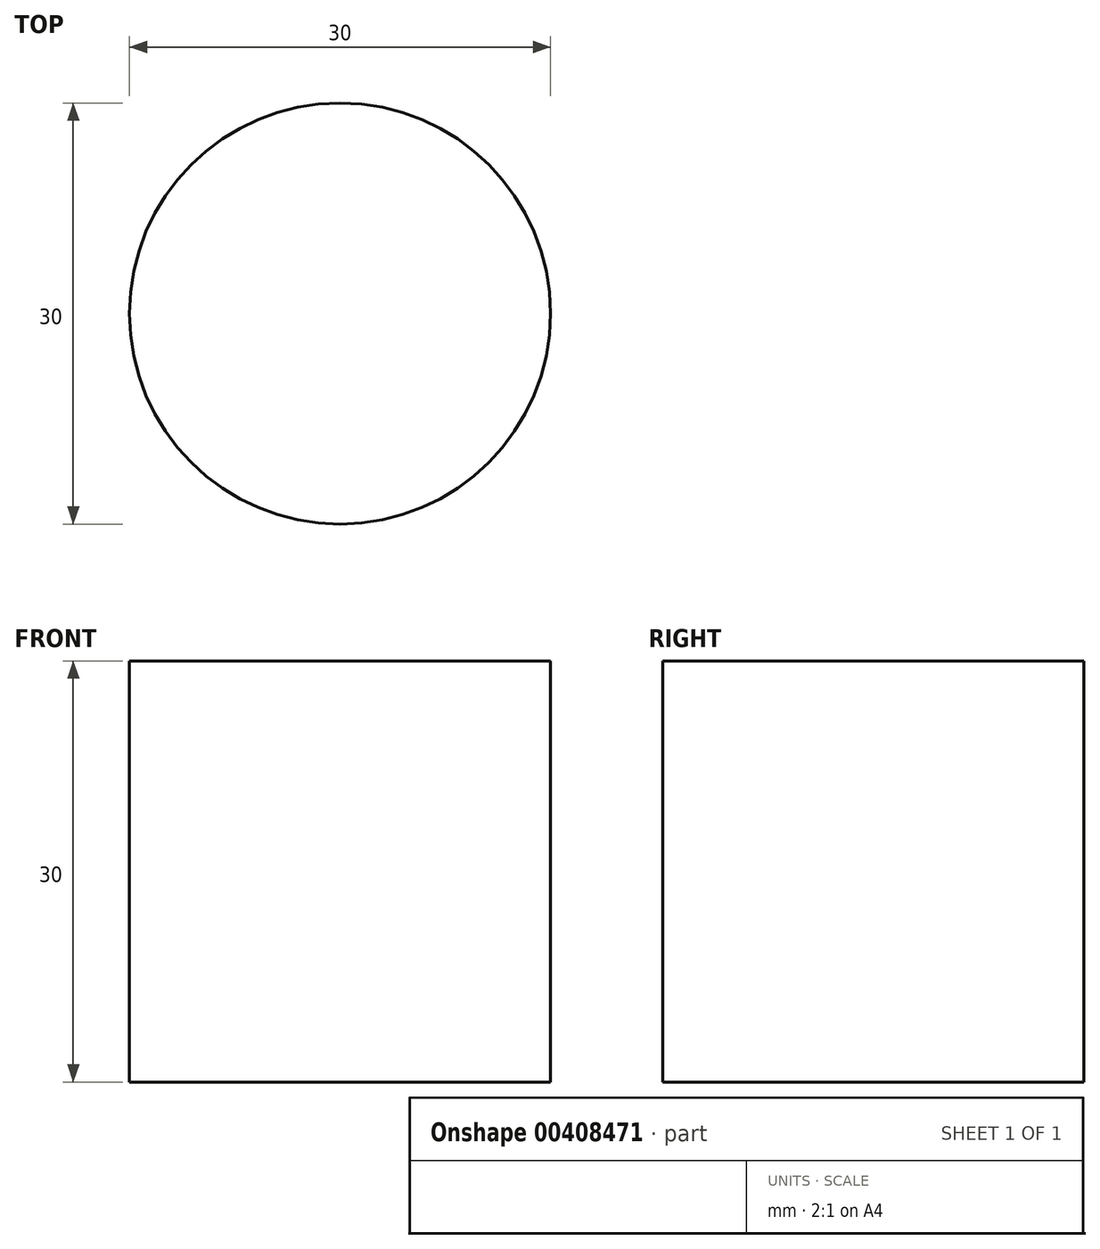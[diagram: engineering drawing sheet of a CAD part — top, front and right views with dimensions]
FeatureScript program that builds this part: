
annotation { "Feature Type Name" : "Feature", "Feature Type Description" : "" }
export const myFeature = defineFeature(function(context is Context, id is Id, definition is map)
    precondition{}
    {
        {
            var Q0;
            Q0=qCreatedBy(makeId("Top.planeOp"),FACE);
            var sketch = newSketch(context, id + "F0", { "sketchPlane" : qUnion([Q0])});
            skCircle(sketch, "E0", {"center": v(0, 0) * mm, "radius": 15 * mm});
            skSolve(sketch);
        }
        {
            var Q0;
            Q0 = qSketchRegion(id + "F0", true);
            extrude(context, id + "F1", {"entities" : qUnion([Q0]), "endBound" : BoundingType.SYMMETRIC, "depth" : 30 * mm});
        }
    });
